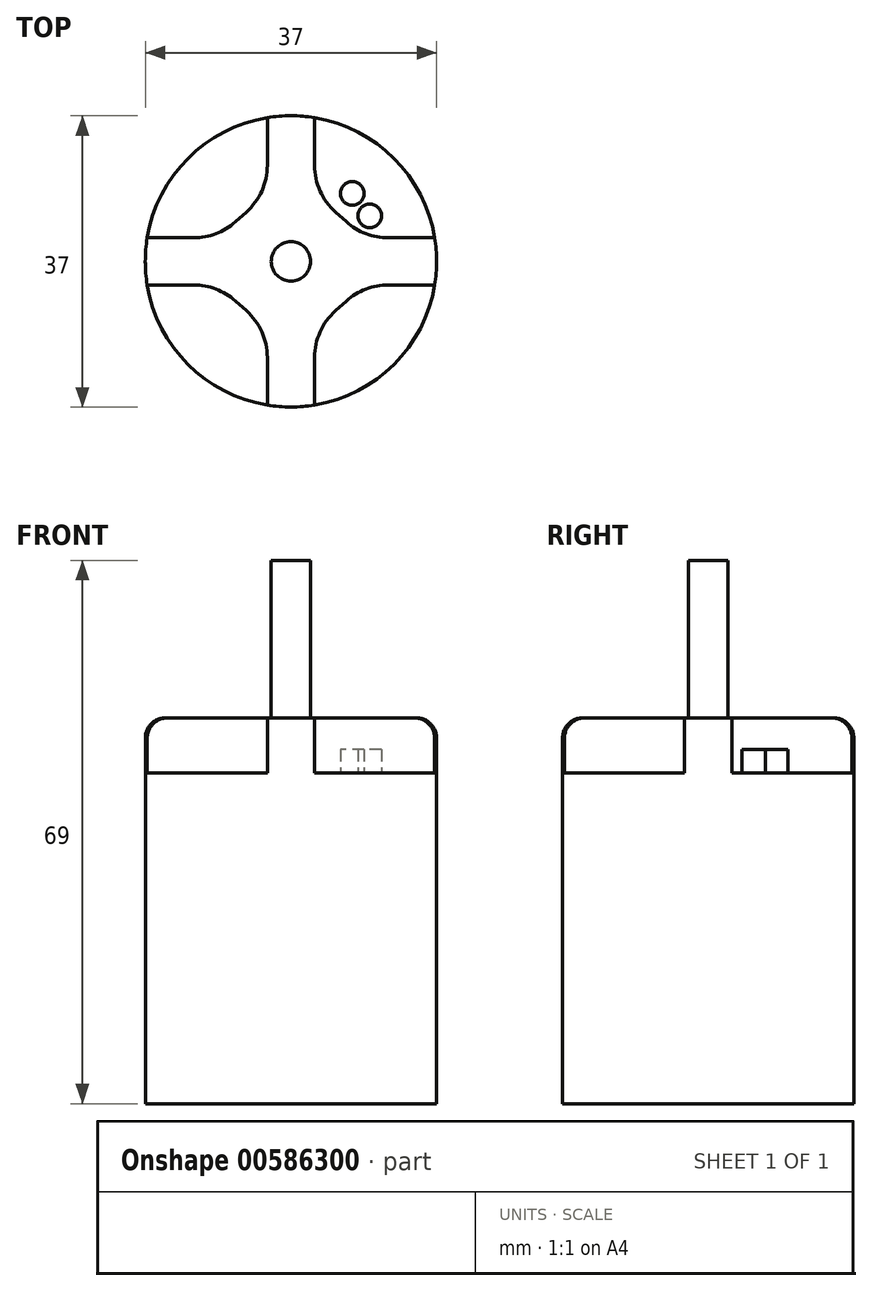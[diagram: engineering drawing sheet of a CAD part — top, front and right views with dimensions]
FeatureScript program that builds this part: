
annotation { "Feature Type Name" : "Feature", "Feature Type Description" : "" }
export const myFeature = defineFeature(function(context is Context, id is Id, definition is map)
    precondition{}
    {
        {
            var Q0;
            Q0=qCreatedBy(makeId("Top.planeOp"),FACE);
            var sketch = newSketch(context, id + "F0", { "sketchPlane" : qUnion([Q0])});
            skCircle(sketch, "E0", {"center": v(0, 0) * mm, "radius": 18.5 * mm});
            skSolve(sketch);
        }
        {
            var Q0;
            Q0=makeQuery(id+"F0.imprint","IMPRINT",FACE,{"disambiguationData":[TD([[makeQuery(id+"F0.imprint","IMPRINT",EDGE,{"derivedFrom":sQuery(id+"F0.wireOp",EDGE,"E0")}),1.0]])]});
            extrude(context, id + "F1", {"entities" : qUnion([Q0]), "depth" : 42 * mm, "offsetDistance" : 25.4 * mm});
        }
        {
            var Q0;
            Q0=makeQuery(id+"F1.opExtrude","CAP_FACE",FACE,{"disambiguationData":[OSD([sQuery(id+"F0.wireOp",EDGE,"E0")])],"isStart":false});
            var sketch = newSketch(context, id + "F2", { "sketchPlane" : qUnion([Q0])});
            skLineSegment(sketch, "E1", {"start": v(-18.26, -3) * mm, "end": v(-12.36, -3) * mm});
            skLineSegment(sketch, "E2", {"start": v(-7.05, -5.02) * mm, "end": v(-5.66, -6.26) * mm});
            skLineSegment(sketch, "E3", {"start": v(-3, -12.2) * mm, "end": v(-3, -18.26) * mm});
            skPoint(sketch, "E4.visualSharp", {"position": v(-9.32, -3) * mm});
            skArc(sketch, "E4.filletArc", {"start": v(-7.05, -5.02) * mm, "mid": v(-9.52, -3.52) * mm, "end": v(-12.36, -3) * mm});
            skPoint(sketch, "E5.visualSharp", {"position": v(-3, -8.64) * mm});
            skArc(sketch, "E5.filletArc", {"start": v(-3, -12.2) * mm, "mid": v(-3.7, -8.95) * mm, "end": v(-5.66, -6.26) * mm});
            skLineSegment(sketch, "E6.MirrorCS", {"start": v(3, -12.2) * mm, "end": v(3, -18.26) * mm});
            skArc(sketch, "E7.MirrorCS", {"start": v(3, -12.2) * mm, "mid": v(3.7, -8.95) * mm, "end": v(5.66, -6.26) * mm});
            skLineSegment(sketch, "E8.MirrorCS", {"start": v(7.05, -5.02) * mm, "end": v(5.66, -6.26) * mm});
            skArc(sketch, "E9.MirrorCS", {"start": v(7.05, -5.02) * mm, "mid": v(9.52, -3.52) * mm, "end": v(12.36, -3) * mm});
            skLineSegment(sketch, "E10.MirrorCS", {"start": v(18.26, -3) * mm, "end": v(12.36, -3) * mm});
            skLineSegment(sketch, "E11.MirrorCS", {"start": v(-18.26, 3) * mm, "end": v(-12.36, 3) * mm});
            skArc(sketch, "E12.MirrorCS", {"start": v(-7.05, 5.02) * mm, "mid": v(-9.52, 3.52) * mm, "end": v(-12.36, 3) * mm});
            skLineSegment(sketch, "E13.MirrorCS", {"start": v(-7.05, 5.02) * mm, "end": v(-5.66, 6.26) * mm});
            skArc(sketch, "E14.MirrorCS", {"start": v(-3, 12.2) * mm, "mid": v(-3.7, 8.95) * mm, "end": v(-5.66, 6.26) * mm});
            skLineSegment(sketch, "E15.MirrorCS", {"start": v(-3, 12.2) * mm, "end": v(-3, 18.26) * mm});
            skLineSegment(sketch, "E16.MirrorCS", {"start": v(3, 12.2) * mm, "end": v(3, 18.26) * mm});
            skArc(sketch, "E17.MirrorCS", {"start": v(3, 12.2) * mm, "mid": v(3.7, 8.95) * mm, "end": v(5.66, 6.26) * mm});
            skLineSegment(sketch, "E18.MirrorCS", {"start": v(7.05, 5.02) * mm, "end": v(5.66, 6.26) * mm});
            skArc(sketch, "E19.MirrorCS", {"start": v(7.05, 5.02) * mm, "mid": v(9.52, 3.52) * mm, "end": v(12.36, 3) * mm});
            skLineSegment(sketch, "E20.MirrorCS", {"start": v(18.26, 3) * mm, "end": v(12.36, 3) * mm});
            skPoint(sketch, "E21.orphan", {"position": v(-18.5, 0) * mm});
            skPoint(sketch, "E22.orphan", {"position": v(0, 18.5) * mm});
            skSolve(sketch);
        }
        {
            var Q0;
            {var subQ3=sQuery(id+"F2.wireOp",EDGE,"E1");Q0=makeQuery(id+"F2.imprint","IMPRINT",FACE,{"disambiguationData":[TD([[makeQuery(id+"F2.imprint","IMPRINT",EDGE,{"derivedFrom":subQ3}),1.0]])]});}
            extrude(context, id + "F3", {"entities" : qUnion([Q0]), "operationType" : NewBodyOperationType.ADD, "depth" : 7 * mm, "offsetDistance" : 25.4 * mm});
        }
        {
            var Q0;
            {var subQ0=sQuery(id+"F0.wireOp",EDGE,"E0");var subQ1=makeQuery(id+"F1.opExtrude","CAP_EDGE",EDGE,{"disambiguationData":[OSD([subQ0])],"isStart":false});Q0=makeQuery(id+"F3.opExtrude","CAP_EDGE",EDGE,{"disambiguationData":[OSD([subQ0]),TDD([makeQuery(id+"F2.imprint","IMPRINT",EDGE,{"disambiguationData":[TD([[makeQuery(id+"F2.imprint","INTERSECT",VERTEX,{"derivedFrom":[subQ1,sQuery(id+"F2.wireOp",EDGE,"E15.MirrorCS")]}),1.0]])],"derivedFrom":subQ1})])],"isStart":false});}
            var Q1;
            {var subQ0=sQuery(id+"F0.wireOp",EDGE,"E0");var subQ1=makeQuery(id+"F1.opExtrude","CAP_EDGE",EDGE,{"disambiguationData":[OSD([subQ0])],"isStart":false});Q1=makeQuery(id+"F3.opExtrude","CAP_EDGE",EDGE,{"disambiguationData":[OSD([subQ0]),TDD([makeQuery(id+"F2.imprint","IMPRINT",EDGE,{"disambiguationData":[TD([[makeQuery(id+"F2.imprint","INTERSECT",VERTEX,{"derivedFrom":[subQ1,sQuery(id+"F2.wireOp",EDGE,"E1")]}),1.0]])],"derivedFrom":subQ1})])],"isStart":false});}
            var Q2;
            {var subQ0=sQuery(id+"F0.wireOp",EDGE,"E0");var subQ1=makeQuery(id+"F1.opExtrude","CAP_EDGE",EDGE,{"disambiguationData":[OSD([subQ0])],"isStart":false});Q2=makeQuery(id+"F3.opExtrude","CAP_EDGE",EDGE,{"disambiguationData":[OSD([subQ0]),TDD([makeQuery(id+"F2.imprint","IMPRINT",EDGE,{"disambiguationData":[TD([[makeQuery(id+"F2.imprint","INTERSECT",VERTEX,{"derivedFrom":[subQ1,sQuery(id+"F2.wireOp",EDGE,"E3")]}),-1.0]])],"derivedFrom":subQ1})])],"isStart":false});}
            var Q3;
            {var subQ0=sQuery(id+"F0.wireOp",EDGE,"E0");var subQ1=makeQuery(id+"F1.opExtrude","CAP_EDGE",EDGE,{"disambiguationData":[OSD([subQ0])],"isStart":false});Q3=makeQuery(id+"F3.opExtrude","CAP_EDGE",EDGE,{"disambiguationData":[OSD([subQ0]),TDD([makeQuery(id+"F2.imprint","IMPRINT",EDGE,{"disambiguationData":[TD([[makeQuery(id+"F2.imprint","INTERSECT",VERTEX,{"derivedFrom":[subQ1,sQuery(id+"F2.wireOp",EDGE,"E10.MirrorCS")]}),-1.0]])],"derivedFrom":subQ1})])],"isStart":false});}
            fillet(context, id + "F4", {"entities" : qUnion([Q0, Q1, Q2, Q3]), "radius" : 2.54 * mm, "tangentPropagation" : true, "allowEdgeOverflow" : false});
        }
        {
            var Q0;
            Q0=makeQuery(id+"F3.opExtrude","CAP_FACE",FACE,{"disambiguationData":[OSD([sQuery(id+"F0.wireOp",EDGE,"E0"),sQuery(id+"F2.wireOp",EDGE,"E1"),sQuery(id+"F2.wireOp",EDGE,"E2"),sQuery(id+"F2.wireOp",EDGE,"E3"),sQuery(id+"F2.wireOp",EDGE,"E4.filletArc"),sQuery(id+"F2.wireOp",EDGE,"E5.filletArc"),sQuery(id+"F2.wireOp",EDGE,"E6.MirrorCS"),sQuery(id+"F2.wireOp",EDGE,"E7.MirrorCS"),sQuery(id+"F2.wireOp",EDGE,"E8.MirrorCS"),sQuery(id+"F2.wireOp",EDGE,"E9.MirrorCS"),sQuery(id+"F2.wireOp",EDGE,"E10.MirrorCS"),sQuery(id+"F2.wireOp",EDGE,"E11.MirrorCS"),sQuery(id+"F2.wireOp",EDGE,"E12.MirrorCS"),sQuery(id+"F2.wireOp",EDGE,"E13.MirrorCS"),sQuery(id+"F2.wireOp",EDGE,"E14.MirrorCS"),sQuery(id+"F2.wireOp",EDGE,"E15.MirrorCS"),sQuery(id+"F2.wireOp",EDGE,"E16.MirrorCS"),sQuery(id+"F2.wireOp",EDGE,"E17.MirrorCS"),sQuery(id+"F2.wireOp",EDGE,"E18.MirrorCS"),sQuery(id+"F2.wireOp",EDGE,"E19.MirrorCS"),sQuery(id+"F2.wireOp",EDGE,"E20.MirrorCS")])],"isStart":false});
            var sketch = newSketch(context, id + "F5", { "sketchPlane" : qUnion([Q0])});
            skCircle(sketch, "E23", {"center": v(0, 0) * mm, "radius": 2.5 * mm});
            skSolve(sketch);
        }
        {
            var Q0;
            Q0=makeQuery(id+"F5.imprint","IMPRINT",FACE,{"disambiguationData":[TD([[makeQuery(id+"F5.imprint","IMPRINT",EDGE,{"derivedFrom":sQuery(id+"F5.wireOp",EDGE,"E23")}),1.0]])]});
            extrude(context, id + "F6", {"entities" : qUnion([Q0]), "operationType" : NewBodyOperationType.ADD, "depth" : 20 * mm, "offsetDistance" : 25.4 * mm});
        }
        {
            var Q0;
            {var subQ0=sQuery(id+"F2.wireOp",EDGE,"E16.MirrorCS");var subQ1=sQuery(id+"F0.wireOp",EDGE,"E0");Q0=makeQuery(id+"F3.boolean.opBoolean","SPLIT",FACE,{"disambiguationData":[TD([makeQuery(id+"F3.opExtrude","SWEPT_FACE",FACE,{"disambiguationData":[OSD([subQ0])]})])],"derivedFrom":makeQuery(id+"F1.opExtrude","CAP_FACE",FACE,{"disambiguationData":[OSD([subQ1])],"isStart":false})});}
            var sketch = newSketch(context, id + "F7", { "sketchPlane" : qUnion([Q0])});
            skCircle(sketch, "E24", {"center": v(10, 5.78) * mm, "radius": 1.5 * mm});
            skCircle(sketch, "E25", {"center": v(7.8, 8.64) * mm, "radius": 1.5 * mm});
            skCircle(sketch, "E26", {"center": v(6.19, 11.97) * mm, "radius": 1.5 * mm});
            skSolve(sketch);
        }
        {
            var Q0;
            Q0=makeQuery(id+"F7.imprint","IMPRINT",FACE,{"disambiguationData":[TD([[makeQuery(id+"F7.imprint","IMPRINT",EDGE,{"derivedFrom":sQuery(id+"F7.wireOp",EDGE,"E26")}),1.0]])]});
            var sketch = newSketch(context, id + "F8", { "sketchPlane" : qUnion([Q0])});
            skSolve(sketch);
        }
        {
            var Q0;
            Q0 = qSketchRegion(id + "F8", true);
            var Q1;
            Q1=makeQuery(id+"F8.imprint","IMPRINT",FACE,{"disambiguationData":[TD([[makeQuery(id+"F8.imprint","IMPRINT",EDGE,{"derivedFrom":makeQuery(id+"F7.imprint","IMPRINT",EDGE,{"derivedFrom":sQuery(id+"F7.wireOp",EDGE,"E26")})}),1.0]])]});
            var Q2;
            Q2=makeQuery(id+"F7.imprint","IMPRINT",FACE,{"disambiguationData":[TD([[makeQuery(id+"F7.imprint","IMPRINT",EDGE,{"derivedFrom":sQuery(id+"F7.wireOp",EDGE,"E25")}),1.0]])]});
            var Q3;
            Q3=makeQuery(id+"F7.imprint","IMPRINT",FACE,{"disambiguationData":[TD([[makeQuery(id+"F7.imprint","IMPRINT",EDGE,{"derivedFrom":sQuery(id+"F7.wireOp",EDGE,"E24")}),1.0]])]});
            extrude(context, id + "F9", {"entities" : qUnion([Q0, Q1, Q2, Q3]), "operationType" : NewBodyOperationType.ADD, "depth" : 3 * mm, "offsetDistance" : 25.4 * mm});
        }
    });
